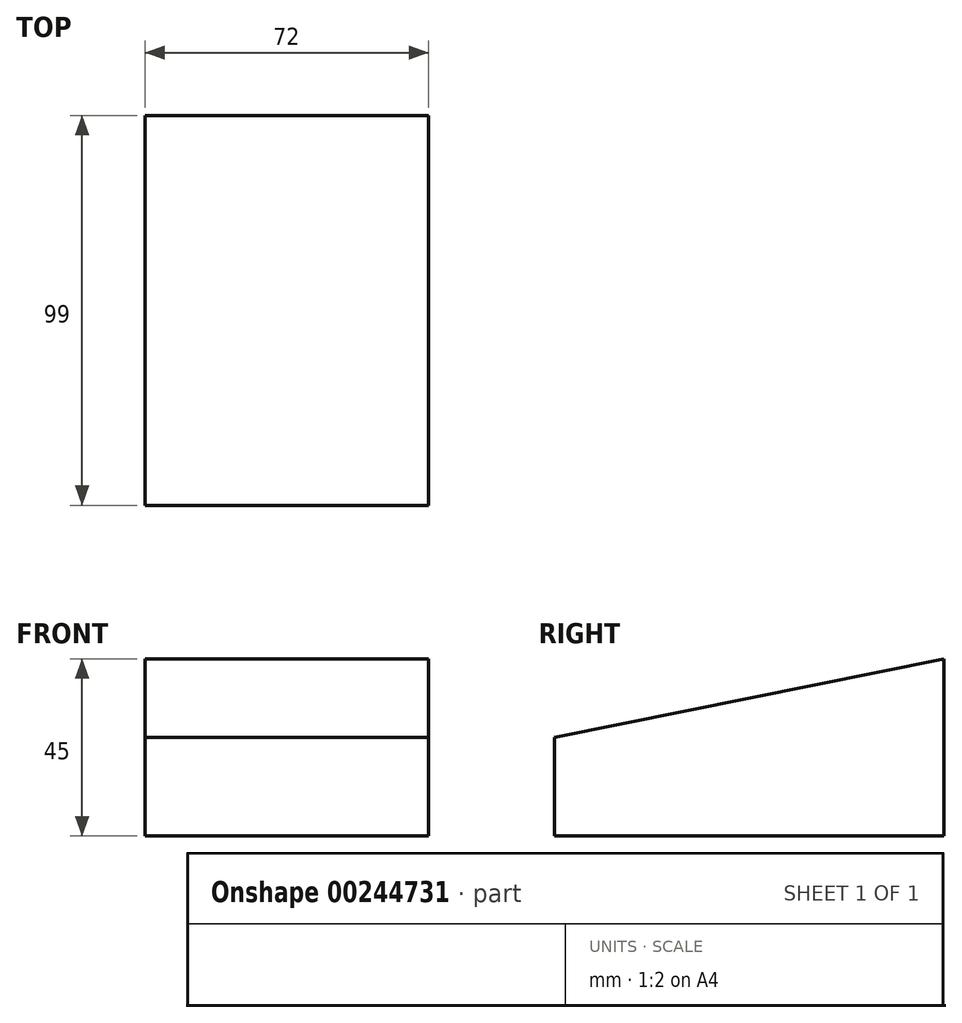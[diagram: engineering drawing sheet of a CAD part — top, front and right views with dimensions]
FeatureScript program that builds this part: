
annotation { "Feature Type Name" : "Feature", "Feature Type Description" : "" }
export const myFeature = defineFeature(function(context is Context, id is Id, definition is map)
    precondition{}
    {
        {
            var Q0;
            Q0=qCreatedBy(makeId("Top.planeOp"),FACE);
            var sketch = newSketch(context, id + "F0", { "sketchPlane" : qUnion([Q0])});
            skLineSegment(sketch, "E0.bottom", {"start": v(-36, 49.5) * mm, "end": v(36, 49.5) * mm});
            skLineSegment(sketch, "E0.top", {"start": v(-36, -49.5) * mm, "end": v(36, -49.5) * mm});
            skLineSegment(sketch, "E0.left", {"start": v(-36, 49.5) * mm, "end": v(-36, -49.5) * mm});
            skLineSegment(sketch, "E0.right", {"start": v(36, 49.5) * mm, "end": v(36, -49.5) * mm});
            skPoint(sketch, "E0.middle", {"position": v(0, 0) * mm});
            skSolve(sketch);
        }
        {
            var Q0;
            Q0=makeQuery(id+"F0.imprint","IMPRINT",FACE,{"disambiguationData":[TD([[makeQuery(id+"F0.imprint","IMPRINT",EDGE,{"derivedFrom":sQuery(id+"F0.wireOp",EDGE,"E0.bottom")}),-1.0]])]});
            extrude(context, id + "F1", {"entities" : qUnion([Q0]), "depth" : 45 * mm});
        }
        {
            var Q0;
            Q0=makeQuery(id+"F1.opExtrude","SWEPT_FACE",FACE,{"disambiguationData":[OSD([sQuery(id+"F0.wireOp",EDGE,"E0.left")])]});
            var sketch = newSketch(context, id + "F2", { "sketchPlane" : qUnion([Q0])});
            skLineSegment(sketch, "E1.bottom", {"start": v(-49.5, 0) * mm, "end": v(49.5, 0) * mm});
            skLineSegment(sketch, "E1.top", {"start": v(-49.5, 25) * mm, "end": v(49.5, 25) * mm});
            skLineSegment(sketch, "E1.left", {"start": v(-49.5, 0) * mm, "end": v(-49.5, 25) * mm});
            skLineSegment(sketch, "E1.right", {"start": v(49.5, 0) * mm, "end": v(49.5, 25) * mm});
            skLineSegment(sketch, "E2", {"start": v(-49.5, 45) * mm, "end": v(49.5, 25) * mm});
            skSolve(sketch);
        }
        {
            var Q0;
            {var subQ0=sQuery(id+"F2.wireOp",EDGE,"E2");Q0=makeQuery(id+"F2.imprint","IMPRINT",FACE,{"disambiguationData":[TD([[makeQuery(id+"F2.imprint","IMPRINT",EDGE,{"derivedFrom":subQ0}),1.0]])]});}
            extrude(context, id + "F3", {"entities" : qUnion([Q0]), "operationType" : NewBodyOperationType.REMOVE, "endBound" : BoundingType.THROUGH_ALL, "oppositeDirection" : true, "depth" : 25 * mm});
        }
    });
